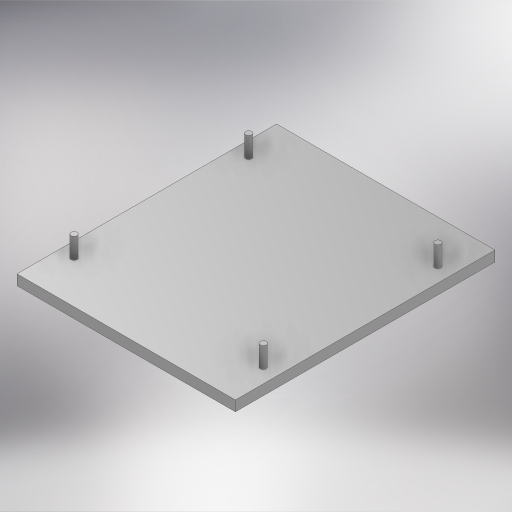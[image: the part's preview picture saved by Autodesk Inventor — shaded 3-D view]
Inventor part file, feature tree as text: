
AUTODESK INVENTOR PART (.ipt)
format: ipt  version: 2024 (Build 280153000, 153)  size: 350,208 bytes
history: native  units: mm
features: other x11, extrude x3, sketch x3
ambient origin geometry x8: Origin, YZ Plane, XZ Plane, XY Plane, X Axis, Y Axis, Z Axis, Center Point
bodies: Body1 (feature_tree)
feature tree (17):
  other  "Sólido1"
  extrude  "Extrusión1"  Depth=126.0mm
  extrude  "Extrusión2"  Depth=53.0mm
  extrude  "Extrusión3"  Depth=3.0mm
  sketch  "Boceto1"  dims[d1=106.0mm d2=126.0mm]
  sketch  "Boceto2"  dims[d3=53.0mm d4=63.0mm]
  sketch  "Boceto3"  dims[d5=5.0mm d6=0.0mm d7=3.0mm d8=20.616mm d9=7.071mm d10=10.0mm d11=0.0mm d12=52.5mm d13=126.0mm d14=106.0mm d15=52.5mm d16=35.0mm d17=35.0mm d18=35.0mm d19=35.0mm d20=35.0mm d21=2.0mm d22=0.0mm]
  other  "Finish1"
  other  "Finish2"
  other  "Finish3"
  other  "Finish4"
  other  "Finish5"
  other  "Finish6"
  other  "Finish7"
  other  "Finish8"
  other  "Finish9"
  other  "Finish10"
